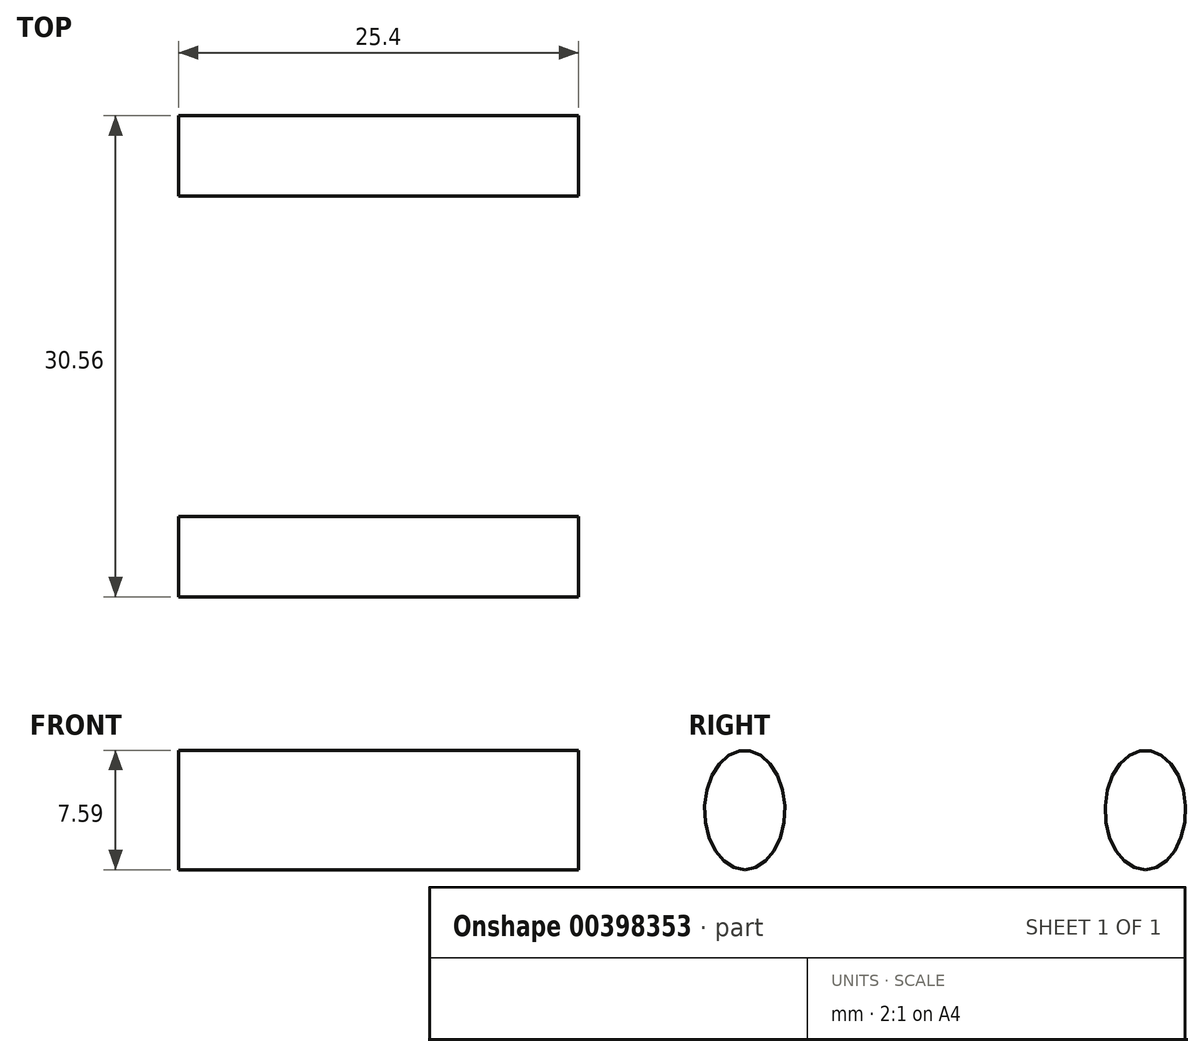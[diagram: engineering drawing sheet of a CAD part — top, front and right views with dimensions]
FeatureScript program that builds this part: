
annotation { "Feature Type Name" : "Feature", "Feature Type Description" : "" }
export const myFeature = defineFeature(function(context is Context, id is Id, definition is map)
    precondition{}
    {
        {
            var Q0;
            Q0=qCreatedBy(makeId("Right.planeOp"),FACE);
            var sketch = newSketch(context, id + "F0", { "sketchPlane" : qUnion([Q0])});
            skEllipse(sketch, "E0", {"center": v(12.72, 7.62) * mm, "majorRadius": 3.8 * mm, "minorRadius": 2.56 * mm, "majorAxis": v(0, -1)});
            skLineSegment(sketch, "E1", {"start": v(0, -10.6) * mm, "end": v(0, 21.69) * mm});
            skEllipse(sketch, "E2.MirrorC", {"center": v(-12.72, 7.62) * mm, "majorRadius": 3.8 * mm, "minorRadius": 2.56 * mm, "majorAxis": v(0, -1)});
            skSolve(sketch);
        }
        {
            var Q0;
            Q0=makeQuery(id+"F0.imprint","IMPRINT",FACE,{"disambiguationData":[TD([[makeQuery(id+"F0.imprint","IMPRINT",EDGE,{"derivedFrom":sQuery(id+"F0.wireOp",EDGE,"E2.MirrorC")}),1.0]])]});
            var Q1;
            Q1=makeQuery(id+"F0.imprint","IMPRINT",FACE,{"disambiguationData":[TD([[makeQuery(id+"F0.imprint","IMPRINT",EDGE,{"derivedFrom":sQuery(id+"F0.wireOp",EDGE,"E0")}),1.0]])]});
            extrude(context, id + "F1", {"entities" : qUnion([Q0, Q1]), "depth" : 25.4 * mm});
        }
    });
